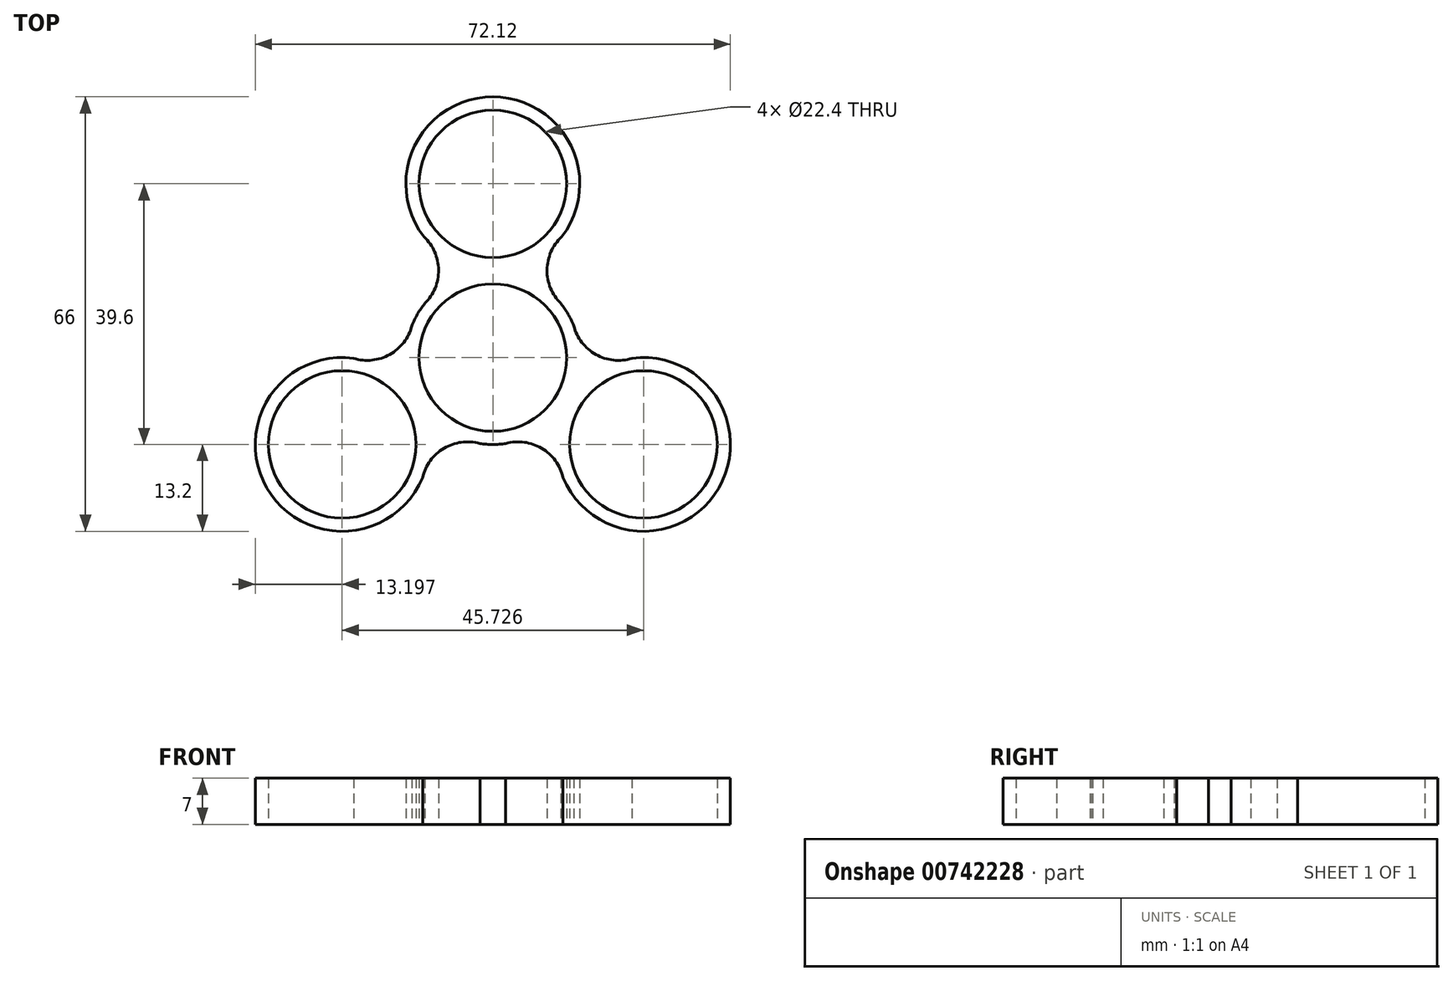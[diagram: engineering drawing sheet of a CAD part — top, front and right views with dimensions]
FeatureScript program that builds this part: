
annotation { "Feature Type Name" : "Feature", "Feature Type Description" : "" }
export const myFeature = defineFeature(function(context is Context, id is Id, definition is map)
    precondition{}
    {
        {
            var Q0;
            Q0=qCreatedBy(makeId("Top.planeOp"),FACE);
            var sketch = newSketch(context, id + "F0", { "sketchPlane" : qUnion([Q0])});
            skCircle(sketch, "E0", {"center": v(0, 26.4) * mm, "radius": 11.2 * mm});
            skCircle(sketch, "E1", {"center": v(0, 0) * mm, "radius": 11.2 * mm});
            skArc(sketch, "E2", {"start": v(9.48, 17.21) * mm, "mid": v(0, 39.6) * mm, "end": v(-9.48, 17.21) * mm});
            skArc(sketch, "E3", {"start": v(-9.6, 9.06) * mm, "mid": v(-11.43, 6.6) * mm, "end": v(-12.65, 3.78) * mm});
            skArc(sketch, "E4", {"start": v(-10.32, 8.23) * mm, "mid": v(-8.23, 13.31) * mm, "end": v(-10.45, 18.34) * mm});
            skArc(sketch, "E5", {"start": v(10.45, 18.34) * mm, "mid": v(8.23, 13.31) * mm, "end": v(10.32, 8.23) * mm});
            skCircle(sketch, "E6.1.0", {"center": v(-22.86, -13.2) * mm, "radius": 11.2 * mm});
            skArc(sketch, "E6.1.1", {"start": v(-19.64, -0.4) * mm, "mid": v(-34.3, -19.8) * mm, "end": v(-10.17, -16.81) * mm});
            skArc(sketch, "E6.1.2", {"start": v(-21.1, -0.12) * mm, "mid": v(-15.64, 0.47) * mm, "end": v(-12.29, 4.82) * mm});
            skArc(sketch, "E6.1.3", {"start": v(-1.97, -13.05) * mm, "mid": v(-7.42, -13.78) * mm, "end": v(-10.66, -18.22) * mm});
            skCircle(sketch, "E6.2.0", {"center": v(22.86, -13.2) * mm, "radius": 11.2 * mm});
            skArc(sketch, "E6.2.1", {"start": v(10.17, -16.81) * mm, "mid": v(34.3, -19.8) * mm, "end": v(19.64, -0.4) * mm});
            skArc(sketch, "E6.2.2", {"start": v(10.66, -18.22) * mm, "mid": v(7.42, -13.78) * mm, "end": v(1.97, -13.05) * mm});
            skArc(sketch, "E6.2.3", {"start": v(12.29, 4.82) * mm, "mid": v(15.64, 0.47) * mm, "end": v(21.1, -0.12) * mm});
            skArc(sketch, "E7.trimOffspring", {"start": v(-3.05, -12.84) * mm, "mid": v(0, -13.2) * mm, "end": v(3.05, -12.84) * mm});
            skArc(sketch, "E8.trimOffspring", {"start": v(12.65, 3.78) * mm, "mid": v(11.43, 6.6) * mm, "end": v(9.6, 9.06) * mm});
            skSolve(sketch);
        }
        {
            var Q0;
            Q0=makeQuery(id+"F0.imprint","IMPRINT",FACE,{"disambiguationData":[TD([[makeQuery(id+"F0.imprint","IMPRINT",EDGE,{"derivedFrom":sQuery(id+"F0.wireOp",EDGE,"E0")}),-1.0]])]});
            extrude(context, id + "F1", {"entities" : qUnion([Q0]), "depth" : 7 * mm, "offsetDistance" : 25 * mm});
        }
    });
